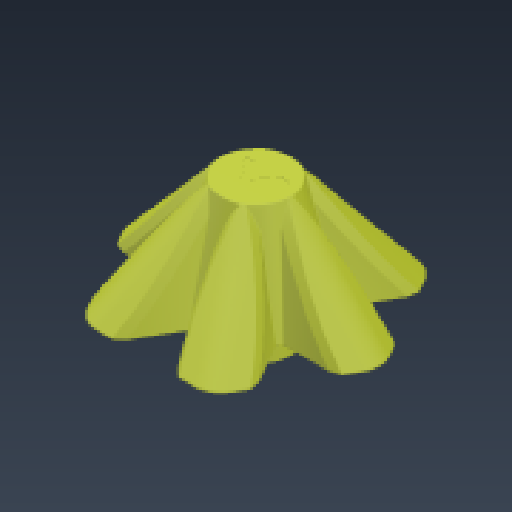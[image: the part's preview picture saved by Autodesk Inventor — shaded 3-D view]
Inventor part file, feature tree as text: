
AUTODESK INVENTOR PART (.ipt)
format: ipt  version: 2024.3 (Build 283343000, 343)  size: 4,723,712 bytes
history: native  units: in
note: dims shown in document units (in); Inventor stores cm internally (conversion verified against a paired STEP export)
features: fillet x1
ambient origin geometry x8: Origin, YZ Plane, XZ Plane, XY Plane, X Axis, Y Axis, Z Axis, Center Point
bodies: Solid1 (feature_tree)
feature tree (1):
  fillet  "Fillet156"  [1 undecoded]
note: 1 required parameter value undecoded (feature->parameter linkage not recoverable at this tier; creation-order binding heuristic only, values carry confidence <= 0.55)
